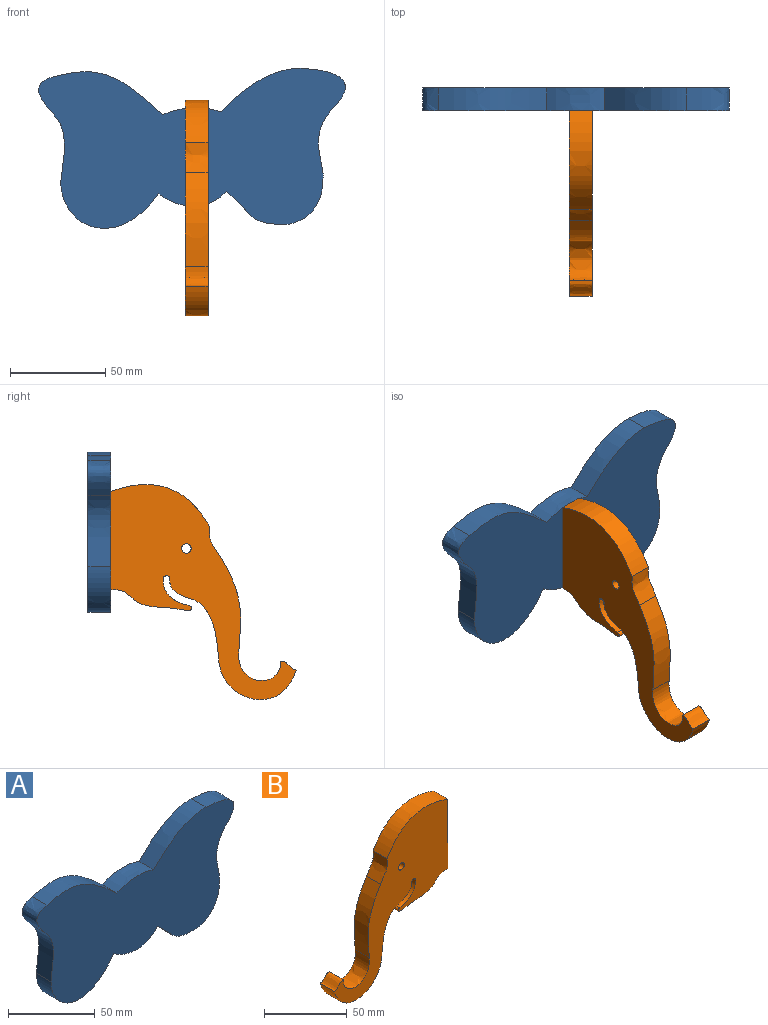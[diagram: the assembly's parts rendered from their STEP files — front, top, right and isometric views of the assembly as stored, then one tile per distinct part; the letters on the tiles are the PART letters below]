
ASSEMBLY  parts=2 mates=1
PART A: 13 faces, bbox 167.3x12x88.3 mm
  f0: extruded ~56.85x22.47mm, area 769.2mm2, adj f1,f10,f11,f12
  f1: extruded ~18.37x12mm, area 301.7mm2, adj f0,f2,f11,f12
  f2: extruded ~37.33x12mm, area 471.8mm2, adj f1,f3,f11,f12
  f3: extruded ~51.37x23.87mm, area 861.9mm2, adj f2,f4,f11,f12
  f4: extruded ~35.55x12mm, area 473.4mm2, adj f3,f5,f11,f12
  f5: extruded ~29.05x17.4mm, area 425.3mm2, adj f4,f6,f11,f12
  f6: extruded ~23.8x21.55mm, area 433.2mm2, adj f5,f7,f11,f12
  f7: extruded ~39.54x12mm, area 512.7mm2, adj f6,f8,f11,f12
  f8: extruded ~22.66x18.58mm, area 439.2mm2, adj f7,f9,f11,f12
  f9: extruded ~42.85x22.9mm, area 599.9mm2, adj f8,f10,f11,f12
  f10: extruded ~30.12x12mm, area 370.8mm2, adj f0,f9,f11,f12
  f11: plane 167.3x88.34mm, normal (0,-1,0), area 9292.1mm2, adj f0,f1,f2,f3,f4,f5,f6,f7
  f12: plane 167.3x88.34mm, normal (0,1,0), area 9292.1mm2, adj f0,f1,f2,f3,f4,f5,f6,f7
PART B: 18 faces, bbox 97x12x121.7 mm
  f0: extruded ~14.8x12mm, area 205.2mm2, adj f1,f15,f16,f17
  f1: extruded ~12x7.88mm, area 97.2mm2, adj f0,f2,f16,f17
  f2: plane 51.55x12mm, normal (1,0,0), area 618.6mm2, adj f1,f3,f16,f17
  f3: extruded ~51.68x22.17mm, area 732.1mm2, adj f2,f4,f16,f17
  f4: extruded ~15.88x12mm, area 208.9mm2, adj f3,f5,f16,f17
  f5: extruded ~49.47x12mm, area 619.9mm2, adj f4,f6,f16,f17
  f6: extruded ~22.05x15.61mm, area 463.5mm2, adj f5,f7,f16,f17
  f7: extruded ~12x8.02mm, area 116mm2, adj f6,f8,f16,f17
  f8: extruded ~40.71x23.21mm, area 740.3mm2, adj f7,f9,f16,f17
  f9: extruded ~29.94x15.23mm, area 432.6mm2, adj f8,f10,f16,f17
  f10: extruded ~12x10.24mm, area 188.1mm2, adj f9,f11,f16,f17
  f11: extruded ~12x3.48mm, area 67.1mm2, adj f10,f12,f16,f17
  f12: extruded ~13.84x13.59mm, area 257.8mm2, adj f11,f13,f16,f17
  f13: extruded ~12x3.84mm, area 77.8mm2, adj f12,f15,f16,f17
  f14: cylinder r=2.48mm len=12mm, axis (0,1,0), area 187.2mm2, adj f16,f17
  f15: extruded ~15.8x12mm, area 191mm2, adj f0,f13,f16,f17
  f16: plane 121.71x97.01mm, normal (0,-1,0), area 4051.9mm2, adj f0,f1,f2,f3,f4,f5,f6,f7
  f17: plane 121.71x97.01mm, normal (0,1,0), area 4051.9mm2, adj f0,f1,f2,f3,f4,f5,f6,f7
PLACE A t=(52.6,53.31,87.81)mm
PLACE B rot(axis=(0,0,1),90deg) t=(-6.82,78.16,161.75)mm
MATE fastened B.f2 <-> A.f11  axis (0,1,0) through (-0.82,41.31,37.35)mm
